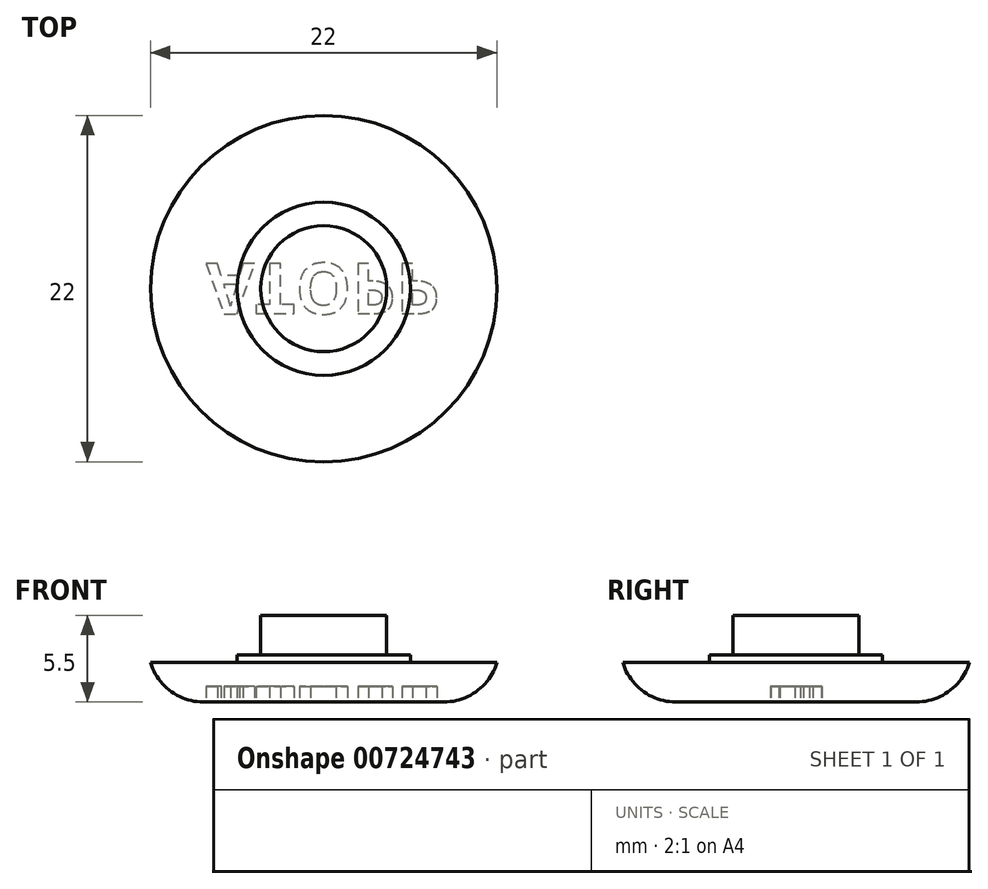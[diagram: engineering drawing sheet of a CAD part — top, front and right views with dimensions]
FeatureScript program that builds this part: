
annotation { "Feature Type Name" : "Feature", "Feature Type Description" : "" }
export const myFeature = defineFeature(function(context is Context, id is Id, definition is map)
    precondition{}
    {
        {
            var Q0;
            Q0=qCreatedBy(makeId("Top.planeOp"),FACE);
            var sketch = newSketch(context, id + "F0", { "sketchPlane" : qUnion([Q0])});
            skCircle(sketch, "E0", {"center": v(0, 0) * mm, "radius": 11 * mm});
            skCircle(sketch, "E1", {"center": v(0, 0) * mm, "radius": 4 * mm});
            skCircle(sketch, "E2", {"center": v(0, 0) * mm, "radius": 5.5 * mm});
            skSolve(sketch);
        }
        {
            var Q0;
            Q0=makeQuery(id+"F0.imprint","IMPRINT",FACE,{"disambiguationData":[TD([[makeQuery(id+"F0.imprint","IMPRINT",EDGE,{"derivedFrom":sQuery(id+"F0.wireOp",EDGE,"E0")}),1.0]])]});
            extrude(context, id + "F1", {"entities" : qUnion([Q0]), "depth" : 2.5 * mm, "offsetDistance" : 25 * mm});
        }
        {
            var Q0;
            Q0=makeQuery(id+"F0.imprint","IMPRINT",FACE,{"disambiguationData":[TD([[makeQuery(id+"F0.imprint","IMPRINT",EDGE,{"derivedFrom":sQuery(id+"F0.wireOp",EDGE,"E1")}),-1.0]])]});
            var Q1;
            Q1=makeQuery(id+"F1.opExtrude","CAP_FACE",FACE,{"disambiguationData":[OSD([sQuery(id+"F0.wireOp",EDGE,"E0"),sQuery(id+"F0.wireOp",EDGE,"E2")])],"isStart":false});
            extrude(context, id + "F2", {"entities" : qUnion([Q0]), "operationType" : NewBodyOperationType.ADD, "endBound" : BoundingType.UP_TO_SURFACE, "depth" : 25 * mm, "endBoundEntityFace" : qUnion([Q1]), "hasOffset" : true, "offsetDistance" : .5 * mm, "offsetOppositeDirection" : true});
        }
        {
            var Q0;
            Q0=makeQuery(id+"F0.imprint","IMPRINT",FACE,{"disambiguationData":[TD([[makeQuery(id+"F0.imprint","IMPRINT",EDGE,{"derivedFrom":sQuery(id+"F0.wireOp",EDGE,"E1")}),1.0]])]});
            var Q1;
            Q1=makeQuery(id+"F2.opExtrude","CAP_FACE",FACE,{"disambiguationData":[OSD([sQuery(id+"F0.wireOp",EDGE,"E0"),sQuery(id+"F0.wireOp",EDGE,"E2")])],"isStart":false});
            extrude(context, id + "F3", {"entities" : qUnion([Q0]), "operationType" : NewBodyOperationType.ADD, "endBound" : BoundingType.UP_TO_SURFACE, "depth" : 3 * mm, "endBoundEntityFace" : qUnion([Q1]), "hasOffset" : true, "offsetDistance" : 2.5 * mm, "offsetOppositeDirection" : true});
        }
        {
            var Q0;
            {var subQ0=sQuery(id+"F0.wireOp",EDGE,"E1");var subQ1=sQuery(id+"F0.wireOp",EDGE,"E2");Q0=makeQuery(id+"F3.boolean.opBoolean","MERGE",FACE,{"derivedFrom":[makeQuery(id+"F2.boolean.opBoolean","MERGE",FACE,{"derivedFrom":[makeQuery(id+"F1.opExtrude","CAP_FACE",FACE,{"disambiguationData":[OSD([sQuery(id+"F0.wireOp",EDGE,"E0"),subQ1])],"isStart":true}),makeQuery(id+"F2.opExtrude","CAP_FACE",FACE,{"disambiguationData":[OSD([subQ0,subQ1])],"isStart":true})]}),makeQuery(id+"F3.opExtrude","CAP_FACE",FACE,{"disambiguationData":[OSD([subQ0])],"isStart":true})]});}
            fillet(context, id + "F4", {"entities" : qUnion([Q0]), "radius" : 3.5 * mm, "tangentPropagation" : true, "allowEdgeOverflow" : false});
        }
        {
            var Q0;
            Q0=qCreatedBy(makeId("Right.planeOp"),FACE);
            var sketch = newSketch(context, id + "F5", { "sketchPlane" : qUnion([Q0])});
            skEllipse(sketch, "E3", {"center": v(-63.43, -1.89) * mm, "majorRadius": 11 * mm, "minorRadius": 2.5 * mm, "majorAxis": v(-1, 0)});
            skPoint(sketch, "E4", {"position": v(-63.43, 0.61) * mm});
            skLineSegment(sketch, "E5", {"start": v(-55.79, 0) * mm, "end": v(-71.08, 0) * mm});
            skArc(sketch, "E6", {"start": v(4.15, 3.3) * mm, "mid": v(11.14, 3.63) * mm, "end": v(4.15, 3.44) * mm});
            skArc(sketch, "E7", {"start": v(-11.15, 3.45) * mm, "mid": v(-11.14, 3.38) * mm, "end": v(-11.14, 3.3) * mm});
            skLineSegment(sketch, "E8", {"start": v(-63.43, 0.61) * mm, "end": v(-63.43, -4.39) * mm});
            skPoint(sketch, "E9.orphan", {"position": v(-63.43, -3.78) * mm});
            skPoint(sketch, "E10.orphan", {"position": v(-63.43, 0) * mm});
            skSolve(sketch);
        }
        {
            var Q0;
            {var subQ0=sQuery(id+"F0.wireOp",EDGE,"E1");var subQ1=sQuery(id+"F0.wireOp",EDGE,"E2");Q0=makeQuery(id+"F3.boolean.opBoolean","MERGE",FACE,{"derivedFrom":[makeQuery(id+"F2.boolean.opBoolean","MERGE",FACE,{"derivedFrom":[makeQuery(id+"F1.opExtrude","CAP_FACE",FACE,{"disambiguationData":[OSD([sQuery(id+"F0.wireOp",EDGE,"E0"),subQ1])],"isStart":true}),makeQuery(id+"F2.opExtrude","CAP_FACE",FACE,{"disambiguationData":[OSD([subQ0,subQ1])],"isStart":true})]}),makeQuery(id+"F3.opExtrude","CAP_FACE",FACE,{"disambiguationData":[OSD([subQ0])],"isStart":true})]});}
            var sketch = newSketch(context, id + "F6", { "sketchPlane" : qUnion([Q0])});
            skText(sketch, "E11", { "text": "ATOPP", "fontName": "OpenSans-Bold.ttf"});
            const initialGuessF6  = {"E11": [-0.00747, -0.00161, 1, 0, 0.00322]};
            skSetInitialGuess(sketch, initialGuessF6);
            skSolve(sketch);
        }
        {
            var Q0;
            Q0=qSketchRegion(id+"F6",true);
            extrude(context, id + "F7", {"entities" : qUnion([Q0]), "operationType" : NewBodyOperationType.REMOVE, "oppositeDirection" : true, "depth" : 1 * mm, "offsetDistance" : 25 * mm});
        }
    });
